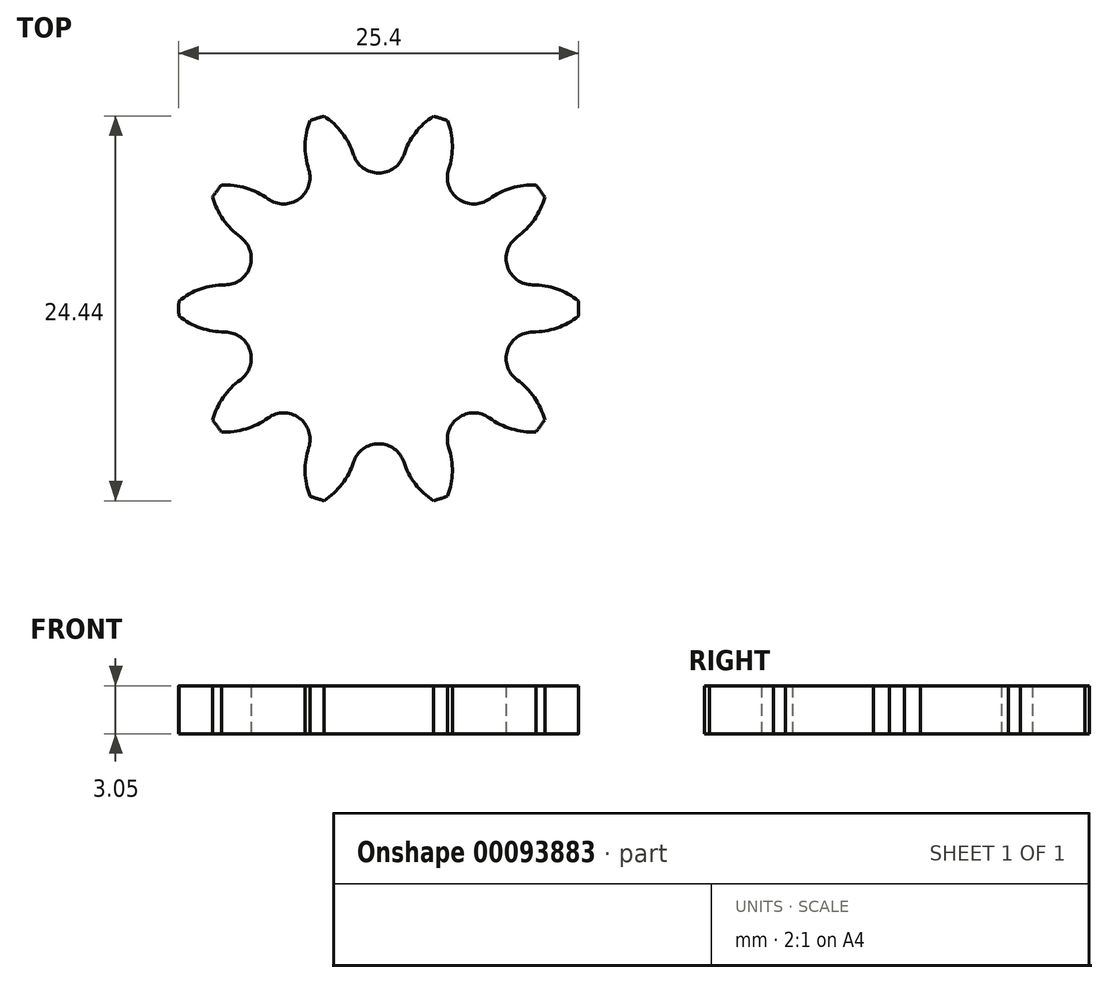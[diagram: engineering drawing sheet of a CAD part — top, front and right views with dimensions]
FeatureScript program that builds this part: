
annotation { "Feature Type Name" : "Feature", "Feature Type Description" : "" }
export const myFeature = defineFeature(function(context is Context, id is Id, definition is map)
    precondition{}
    {
        {
            var Q0;
            Q0=qCreatedBy(makeId("Top.planeOp"),FACE);
            var sketch = newSketch(context, id + "F0", { "sketchPlane" : qUnion([Q0])});
            skCircle(sketch, "E0.cCircle", {"center": v(0, 0) * mm, "radius": 9.77 * mm, "construction": true});
            skLineSegment(sketch, "E0.0", {"start": v(-6.04, 8.31) * mm, "end": v(0, 10.27) * mm, "construction": true});
            skLineSegment(sketch, "E0.1", {"start": v(0, 10.27) * mm, "end": v(6.04, 8.31) * mm, "construction": true});
            skLineSegment(sketch, "E0.2", {"start": v(6.04, 8.31) * mm, "end": v(9.77, 3.17) * mm, "construction": true});
            skLineSegment(sketch, "E0.3", {"start": v(9.77, 3.17) * mm, "end": v(9.77, -3.18) * mm, "construction": true});
            skLineSegment(sketch, "E0.4", {"start": v(9.77, -3.18) * mm, "end": v(6.04, -8.31) * mm, "construction": true});
            skLineSegment(sketch, "E0.5", {"start": v(6.04, -8.31) * mm, "end": v(0, -10.27) * mm, "construction": true});
            skLineSegment(sketch, "E0.6", {"start": v(0, -10.27) * mm, "end": v(-6.04, -8.31) * mm, "construction": true});
            skLineSegment(sketch, "E0.7", {"start": v(-6.04, -8.31) * mm, "end": v(-9.77, -3.17) * mm, "construction": true});
            skLineSegment(sketch, "E0.8", {"start": v(-9.77, -3.17) * mm, "end": v(-9.77, 3.18) * mm, "construction": true});
            skLineSegment(sketch, "E0.9", {"start": v(-9.77, 3.18) * mm, "end": v(-6.04, 8.31) * mm, "construction": true});
            skPoint(sketch, "E0.0.midPoint", {"position": v(-3.02, 9.3) * mm});
            skArc(sketch, "E1", {"start": v(-1.6, 9.76) * mm, "mid": v(-0.99, 8.92) * mm, "end": v(0, 8.6) * mm});
            skArc(sketch, "E2", {"start": v(-5.05, 6.96) * mm, "mid": v(-4.44, 7.8) * mm, "end": v(-4.44, 8.83) * mm});
            skArc(sketch, "E3", {"start": v(-4.44, 8.83) * mm, "mid": v(-4.67, 10.38) * mm, "end": v(-4.37, 11.92) * mm});
            skArc(sketch, "E4", {"start": v(-1.6, 9.76) * mm, "mid": v(-2.32, 11.15) * mm, "end": v(-3.47, 12.22) * mm});
            skArc(sketch, "E5", {"start": v(-4.37, 11.92) * mm, "mid": v(-3.92, 12.08) * mm, "end": v(-3.47, 12.22) * mm});
            skLineSegment(sketch, "E6", {"start": v(0, 0) * mm, "end": v(-6.04, 8.31) * mm});
            skLineSegment(sketch, "E7", {"start": v(0, 0) * mm, "end": v(0, 10.27) * mm});
            skSolve(sketch);
        }
        {
            var Q0;
            {var subQ1=sQuery(id+"F0.wireOp",EDGE,"E1");Q0=makeQuery(id+"F0.imprint","IMPRINT",FACE,{"disambiguationData":[TD([[makeQuery(id+"F0.imprint","IMPRINT",EDGE,{"derivedFrom":subQ1}),-1.0]])]});}
            extrude(context, id + "F1", {"entities" : qUnion([Q0]), "depth" : 3.05 * mm, "offsetDistance" : 25.4 * mm});
        }
        {
            var Q0;
            Q0=makeQuery(id+"F1.opExtrude","SWEPT_BODY",BODY,{"disambiguationData":[OSD([sQuery(id+"F0.wireOp",EDGE,"E1"),sQuery(id+"F0.wireOp",EDGE,"E2"),sQuery(id+"F0.wireOp",EDGE,"E3"),sQuery(id+"F0.wireOp",EDGE,"E4"),sQuery(id+"F0.wireOp",EDGE,"E5"),sQuery(id+"F0.wireOp",EDGE,"E6"),sQuery(id+"F0.wireOp",EDGE,"E7")])]});
            var Q1;
            Q1=makeQuery(id+"F1.opExtrude","SWEPT_EDGE",EDGE,{"disambiguationData":[OSD([sQuery(id+"F0.wireOp",EDGE,"E6"),sQuery(id+"F0.wireOp",EDGE,"E7")])]});
            circularPattern(context, id + "F2", {"operationType" : NewBodyOperationType.ADD, "entities" : qUnion([Q0]), "axis" : qUnion([Q1]), "angle" : 360 * degree, "instanceCount" : 10, "equalSpace" : true});
        }
    });
